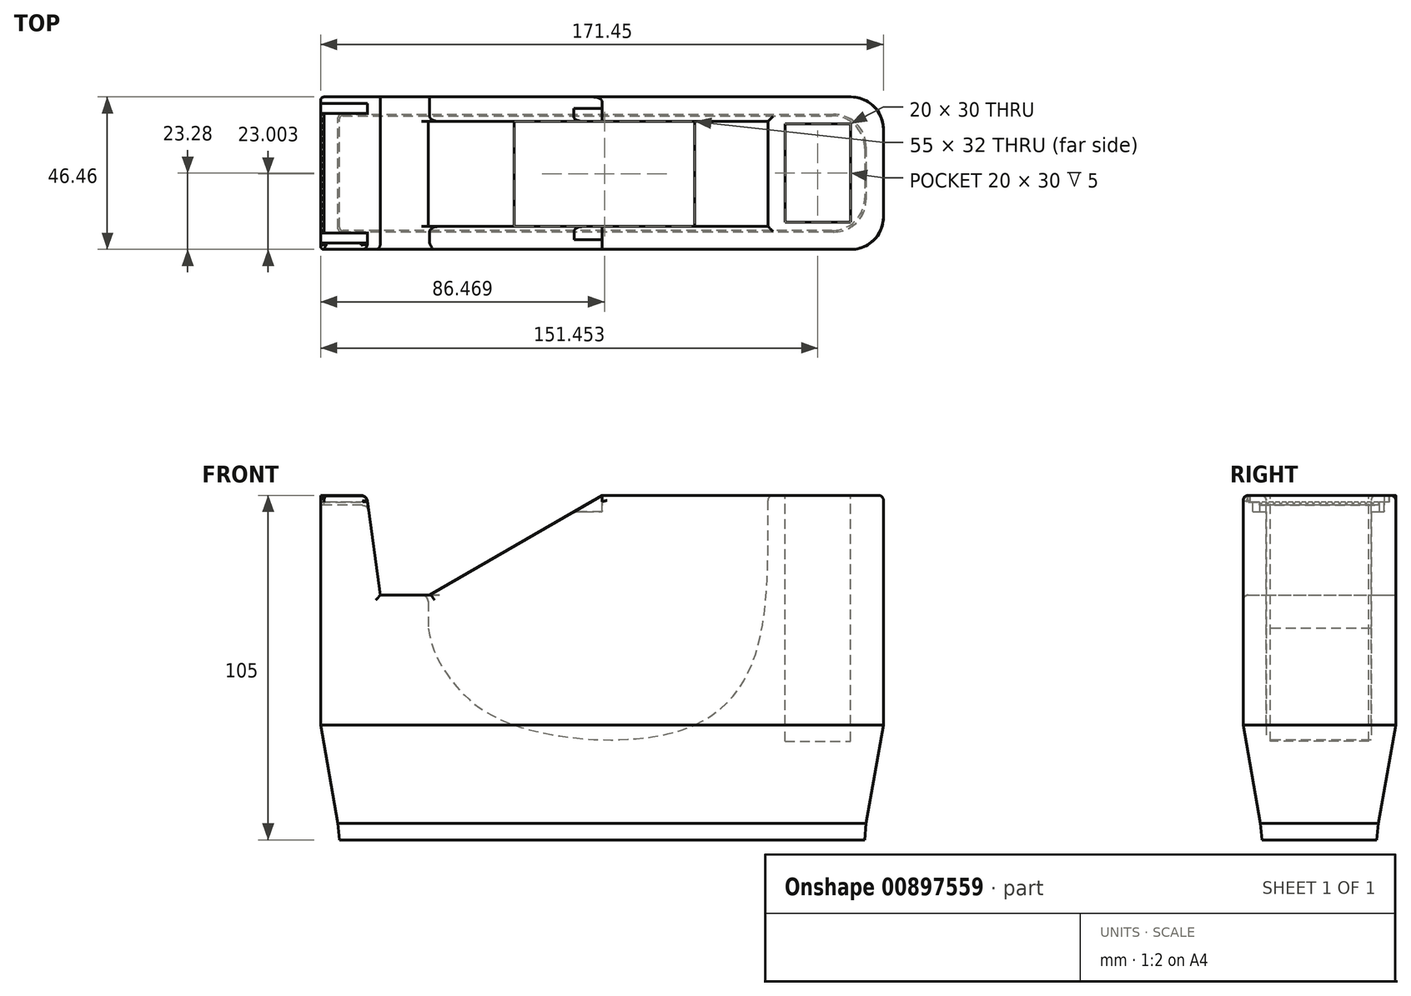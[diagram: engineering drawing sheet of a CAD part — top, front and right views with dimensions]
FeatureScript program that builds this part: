
annotation { "Feature Type Name" : "Feature", "Feature Type Description" : "" }
export const myFeature = defineFeature(function(context is Context, id is Id, definition is map)
    precondition{}
    {
        {
            var Q0;
            Q0=qCreatedBy(makeId("Top.planeOp"),FACE);
            var sketch = newSketch(context, id + "F0", { "sketchPlane" : qUnion([Q0])});
            skLineSegment(sketch, "E0.bottom", {"start": v(-80.11, 15.02) * mm, "end": v(79.89, 15.02) * mm});
            skLineSegment(sketch, "E0.top", {"start": v(-80.11, -19.98) * mm, "end": v(79.89, -19.98) * mm});
            skLineSegment(sketch, "E0.left", {"start": v(-80.11, 15.02) * mm, "end": v(-80.11, -19.98) * mm});
            skLineSegment(sketch, "E0.right", {"start": v(79.89, 15.02) * mm, "end": v(79.89, -19.98) * mm});
            skSolve(sketch);
        }
        {
            var Q0;
            Q0 = qSketchRegion(id + "F0", true);
            extrude(context, id + "F1", {"entities" : qUnion([Q0]), "depth" : 5 * mm, "offsetDistance" : 25 * mm, "hasDraft" : true, "draftAngle" : 5 * degree});
        }
        {
            var Q0;
            Q0=makeQuery(id+"F1.opExtrude","CAP_FACE",FACE,{"disambiguationData":[OSD([sQuery(id+"F0.wireOp",EDGE,"E0.bottom"),sQuery(id+"F0.wireOp",EDGE,"E0.top"),sQuery(id+"F0.wireOp",EDGE,"E0.left"),sQuery(id+"F0.wireOp",EDGE,"E0.right")])],"isStart":false});
            var sketch = newSketch(context, id + "F2", { "sketchPlane" : qUnion([Q0])});
            skLineSegment(sketch, "E1.bottom", {"start": v(-80.55, 15.46) * mm, "end": v(80.32, 15.46) * mm});
            skLineSegment(sketch, "E1.top", {"start": v(-80.55, -20.42) * mm, "end": v(80.32, -20.42) * mm});
            skLineSegment(sketch, "E1.left", {"start": v(-80.55, 15.46) * mm, "end": v(-80.55, -20.42) * mm});
            skLineSegment(sketch, "E1.right", {"start": v(80.32, 15.46) * mm, "end": v(80.32, -20.42) * mm});
            skSolve(sketch);
        }
        {
            var Q0;
            Q0 = qSketchRegion(id + "F2", true);
            extrude(context, id + "F3", {"entities" : qUnion([Q0]), "depth" : 30 * mm, "offsetDistance" : 25 * mm, "hasDraft" : true, "draftAngle" : 10 * degree});
        }
        {
            var Q0;
            Q0=makeQuery(id+"F3.opExtrude","CAP_FACE",FACE,{"disambiguationData":[OSD([sQuery(id+"F2.wireOp",EDGE,"E1.bottom"),sQuery(id+"F2.wireOp",EDGE,"E1.top"),sQuery(id+"F2.wireOp",EDGE,"E1.left"),sQuery(id+"F2.wireOp",EDGE,"E1.right")])],"isStart":false});
            var sketch = newSketch(context, id + "F4", { "sketchPlane" : qUnion([Q0])});
            skLineSegment(sketch, "E2.bottom", {"start": v(85.61, -25.7) * mm, "end": v(-85.84, -25.7) * mm});
            skLineSegment(sketch, "E2.top", {"start": v(85.61, 20.75) * mm, "end": v(-85.84, 20.75) * mm});
            skLineSegment(sketch, "E2.left", {"start": v(85.61, -25.7) * mm, "end": v(85.61, 20.75) * mm});
            skLineSegment(sketch, "E2.right", {"start": v(-85.84, -25.7) * mm, "end": v(-85.84, 20.75) * mm});
            skSolve(sketch);
        }
        {
            var Q0;
            Q0 = qSketchRegion(id + "F4", true);
            extrude(context, id + "F5", {"entities" : qUnion([Q0]), "depth" : 70 * mm, "offsetDistance" : 25 * mm});
        }
        {
            var Q0;
            Q0=makeQuery(id+"F5.opExtrude","SWEPT_FACE",FACE,{"disambiguationData":[OSD([sQuery(id+"F4.wireOp",EDGE,"E2.top")])]});
            var sketch = newSketch(context, id + "F6", { "sketchPlane" : qUnion([Q0])});
            skLineSegment(sketch, "E3", {"start": v(0.11, 105) * mm, "end": v(52.63, 74.68) * mm});
            skLineSegment(sketch, "E4", {"start": v(52.63, 74.68) * mm, "end": v(67.63, 74.68) * mm});
            skLineSegment(sketch, "E5", {"start": v(67.63, 74.68) * mm, "end": v(72.07, 106.96) * mm});
            skLineSegment(sketch, "E6", {"start": v(0.11, 105) * mm, "end": v(0.11, 119.16) * mm});
            skLineSegment(sketch, "E7", {"start": v(0.11, 119.16) * mm, "end": v(72.07, 119.16) * mm});
            skLineSegment(sketch, "E8", {"start": v(72.07, 119.16) * mm, "end": v(72.07, 106.96) * mm});
            skSolve(sketch);
        }
        {
            var Q0;
            Q0 = qSketchRegion(id + "F6", true);
            extrude(context, id + "F7", {"entities" : qUnion([Q0]), "operationType" : NewBodyOperationType.REMOVE, "endBound" : BoundingType.THROUGH_ALL, "oppositeDirection" : true, "depth" : 25 * mm, "offsetDistance" : 25 * mm, "hasDraft" : true, "draftAngle" : 0.1 * degree});
        }
        {
            var Q0;
            {var subQ0=sQuery(id+"F4.wireOp",EDGE,"E2.left");var subQ1=sQuery(id+"F4.wireOp",EDGE,"E2.top");var subQ2=sQuery(id+"F4.wireOp",EDGE,"E2.bottom");Q0=makeQuery(id+"F7.boolean.opBoolean","SPLIT",FACE,{"disambiguationData":[TD([makeQuery(id+"F5.opExtrude","SWEPT_FACE",FACE,{"disambiguationData":[OSD([subQ0])]})])],"derivedFrom":makeQuery(id+"F5.opExtrude","CAP_FACE",FACE,{"disambiguationData":[OSD([subQ2,subQ1,subQ0,sQuery(id+"F4.wireOp",EDGE,"E2.right")])],"isStart":false})});}
            var sketch = newSketch(context, id + "F8", { "sketchPlane" : qUnion([Q0])});
            skLineSegment(sketch, "E9.bottom", {"start": v(55.61, 12.57) * mm, "end": v(75.61, 12.57) * mm});
            skLineSegment(sketch, "E9.top", {"start": v(55.61, -17.43) * mm, "end": v(75.61, -17.43) * mm});
            skLineSegment(sketch, "E9.left", {"start": v(55.61, 12.57) * mm, "end": v(55.61, -17.43) * mm});
            skLineSegment(sketch, "E9.right", {"start": v(75.61, 12.57) * mm, "end": v(75.61, -17.43) * mm});
            skSolve(sketch);
        }
        {
            var Q0;
            Q0 = qSketchRegion(id + "F8", true);
            extrude(context, id + "F9", {"entities" : qUnion([Q0]), "operationType" : NewBodyOperationType.REMOVE, "oppositeDirection" : true, "depth" : 75 * mm, "offsetDistance" : 25 * mm});
        }
        {
            var Q0;
            {var subQ0=sQuery(id+"F4.wireOp",EDGE,"E2.bottom");var subQ1=sQuery(id+"F4.wireOp",EDGE,"E2.right");var subQ2=sQuery(id+"F4.wireOp",EDGE,"E2.top");Q0=makeQuery(id+"F7.boolean.opBoolean","SPLIT",FACE,{"disambiguationData":[TD([makeQuery(id+"F5.opExtrude","SWEPT_FACE",FACE,{"disambiguationData":[OSD([subQ1])]})])],"derivedFrom":makeQuery(id+"F5.opExtrude","CAP_FACE",FACE,{"disambiguationData":[OSD([subQ0,subQ2,sQuery(id+"F4.wireOp",EDGE,"E2.left"),subQ1])],"isStart":false})});}
            var sketch = newSketch(context, id + "F10", { "sketchPlane" : qUnion([Q0])});
            skLineSegment(sketch, "E10.bottom", {"start": v(-71.8, 15.75) * mm, "end": v(-83.4, 15.75) * mm});
            skLineSegment(sketch, "E10.top", {"start": v(-71.7, -20.7) * mm, "end": v(-85.84, -20.7) * mm});
            skLineSegment(sketch, "E11", {"start": v(-83.4, 15.75) * mm, "end": v(-86.58, 15.75) * mm});
            skLineSegment(sketch, "E12", {"start": v(-86.58, 15.75) * mm, "end": v(-86.58, -20.7) * mm});
            skLineSegment(sketch, "E13", {"start": v(-86.58, -20.7) * mm, "end": v(-67.93, -20.7) * mm});
            skLineSegment(sketch, "E14", {"start": v(-67.93, -20.7) * mm, "end": v(-67.93, 15.75) * mm});
            skLineSegment(sketch, "E15", {"start": v(-67.93, 15.75) * mm, "end": v(-71.8, 15.75) * mm});
            skSolve(sketch);
        }
        {
            var Q0;
            Q0 = qSketchRegion(id + "F10", true);
            extrude(context, id + "F11", {"entities" : qUnion([Q0]), "operationType" : NewBodyOperationType.REMOVE, "oppositeDirection" : true, "depth" : 3 * mm, "offsetDistance" : 25 * mm});
        }
        {
            var Q0;
            Q0=makeQuery(id+"F5.opExtrude","SWEPT_FACE",FACE,{"disambiguationData":[OSD([sQuery(id+"F4.wireOp",EDGE,"E2.bottom")])]});
            cPlane(context, id + "F12", {"entities" : qUnion([Q0]), "cplaneType" : CPlaneType.OFFSET, "offset" : 7 * mm, "oppositeDirection" : true, "width" : 150 * mm, "height" : 150 * mm});
        }
        {
            var Q0;
            Q0=qCreatedBy(id+"F12.planeOp",FACE);
            var sketch = newSketch(context, id + "F13", { "sketchPlane" : qUnion([Q0])});
            skLineSegment(sketch, "E16", {"start": v(50.39, 109.97) * mm, "end": v(-53.08, 109.97) * mm});
            skLineSegment(sketch, "E17", {"start": v(-53.08, 109.97) * mm, "end": v(-53.08, 64.4) * mm});
            skFitSpline(sketch, "E18", {"points": [v(-53.08, 64.4) * mm, v(-47.6, 50.9) * mm, v(-30.65, 36.48) * mm, v(24.3, 33.5) * mm, v(46.5, 56.17) * mm, v(50.39, 109.97) * mm], "startDerivative": vector(31.13, -150.45) * mm, "endDerivative": vector(-1.03, 260.97) * mm});
            skSolve(sketch);
        }
        {
            var Q0;
            Q0 = qSketchRegion(id + "F13", true);
            extrude(context, id + "F14", {"entities" : qUnion([Q0]), "operationType" : NewBodyOperationType.REMOVE, "oppositeDirection" : true, "depth" : 32 * mm, "offsetDistance" : 25 * mm});
        }
        {
            var Q0;
            Q0=makeQuery(id+"F14.boolean.opBoolean","COPY",FACE,{"derivedFrom":makeQuery(id+"F14.opExtrude","CAP_FACE",FACE,{"disambiguationData":[OSD([sQuery(id+"F13.wireOp",EDGE,"E16"),sQuery(id+"F13.wireOp",EDGE,"E17"),sQuery(id+"F13.wireOp",EDGE,"E18")])],"isStart":true})});
            var sketch = newSketch(context, id + "F15", { "sketchPlane" : qUnion([Q0])});
            skLineSegment(sketch, "E19", {"start": v(0.05, 105) * mm, "end": v(0.05, 100) * mm});
            skLineSegment(sketch, "E20", {"start": v(0.05, 100) * mm, "end": v(9.05, 100) * mm});
            skLineSegment(sketch, "E21", {"start": v(9.05, 100) * mm, "end": v(9.05, 103) * mm});
            skLineSegment(sketch, "E22", {"start": v(9.05, 103) * mm, "end": v(4.05, 103) * mm});
            skLineSegment(sketch, "E23", {"start": v(4.05, 103) * mm, "end": v(4.05, 105) * mm});
            skLineSegment(sketch, "E24", {"start": v(4.05, 105) * mm, "end": v(0.05, 105) * mm});
            skSolve(sketch);
        }
        {
            var Q0;
            Q0 = qSketchRegion(id + "F15", true);
            extrude(context, id + "F16", {"entities" : qUnion([Q0]), "operationType" : NewBodyOperationType.REMOVE, "oppositeDirection" : true, "depth" : 4 * mm, "offsetDistance" : 25 * mm, "hasSecondDirection" : true, "secondDirectionOppositeDirection" : false, "secondDirectionDepth" : 36 * mm});
        }
        {
            var Q0;
            Q0=makeQuery(id+"F5.opExtrude","SWEPT_FACE",FACE,{"disambiguationData":[OSD([sQuery(id+"F4.wireOp",EDGE,"E2.right")])]});
            var sketch = newSketch(context, id + "F17", { "sketchPlane" : qUnion([Q0])});
            skLineSegment(sketch, "E25", {"start": v(-15.75, 102) * mm, "end": v(-14.75, 105) * mm});
            skPoint(sketch, "E25.endSnap0", {"position": v(2.48, 105) * mm});
            skLineSegment(sketch, "E26", {"start": v(-14.75, 105) * mm, "end": v(-14.75, 102) * mm, "construction": true});
            skLineSegment(sketch, "E27", {"start": v(-15.75, 102) * mm, "end": v(-15.75, 97.68) * mm});
            skLineSegment(sketch, "E28", {"start": v(-15.75, 97.68) * mm, "end": v(20.7, 97.68) * mm});
            skLineSegment(sketch, "E29.MirrorCS", {"start": v(-13.75, 102) * mm, "end": v(-14.75, 105) * mm});
            skLineSegment(sketch, "E30.1.0.0", {"start": v(-11.75, 102) * mm, "end": v(-12.75, 105) * mm});
            skLineSegment(sketch, "E30.1.0.1", {"start": v(-13.75, 102) * mm, "end": v(-12.75, 105) * mm});
            skLineSegment(sketch, "E30.2.0.0", {"start": v(-9.75, 102) * mm, "end": v(-10.75, 105) * mm});
            skLineSegment(sketch, "E30.2.0.1", {"start": v(-11.75, 102) * mm, "end": v(-10.75, 105) * mm});
            skLineSegment(sketch, "E30.direction1", {"start": v(-13.75, 102) * mm, "end": v(-11.75, 102) * mm, "construction": true});
            skLineSegment(sketch, "E31.0.3.0", {"start": v(-7.75, 102) * mm, "end": v(-8.75, 105) * mm});
            skLineSegment(sketch, "E31.3.3.0", {"start": v(-9.75, 102) * mm, "end": v(-8.75, 105) * mm});
            skLineSegment(sketch, "E31.0.4.0", {"start": v(-5.75, 102) * mm, "end": v(-6.75, 105) * mm});
            skLineSegment(sketch, "E31.3.4.0", {"start": v(-7.75, 102) * mm, "end": v(-6.75, 105) * mm});
            skLineSegment(sketch, "E31.0.5.0", {"start": v(-3.75, 102) * mm, "end": v(-4.75, 105) * mm});
            skLineSegment(sketch, "E31.3.5.0", {"start": v(-5.75, 102) * mm, "end": v(-4.75, 105) * mm});
            skLineSegment(sketch, "E31.0.6.0", {"start": v(-1.75, 102) * mm, "end": v(-2.75, 105) * mm});
            skLineSegment(sketch, "E31.3.6.0", {"start": v(-3.75, 102) * mm, "end": v(-2.75, 105) * mm});
            skLineSegment(sketch, "E31.0.7.0", {"start": v(0.25, 102) * mm, "end": v(-0.75, 105) * mm});
            skLineSegment(sketch, "E31.3.7.0", {"start": v(-1.75, 102) * mm, "end": v(-0.75, 105) * mm});
            skLineSegment(sketch, "E31.0.8.0", {"start": v(2.25, 102) * mm, "end": v(1.25, 105) * mm});
            skLineSegment(sketch, "E31.3.8.0", {"start": v(0.25, 102) * mm, "end": v(1.25, 105) * mm});
            skLineSegment(sketch, "E31.0.9.0", {"start": v(4.25, 102) * mm, "end": v(3.25, 105) * mm});
            skLineSegment(sketch, "E31.3.9.0", {"start": v(2.25, 102) * mm, "end": v(3.25, 105) * mm});
            skLineSegment(sketch, "E31.0.10.0", {"start": v(6.25, 102) * mm, "end": v(5.25, 105) * mm});
            skLineSegment(sketch, "E31.3.10.0", {"start": v(4.25, 102) * mm, "end": v(5.25, 105) * mm});
            skLineSegment(sketch, "E31.0.11.0", {"start": v(8.25, 102) * mm, "end": v(7.25, 105) * mm});
            skLineSegment(sketch, "E31.3.11.0", {"start": v(6.25, 102) * mm, "end": v(7.25, 105) * mm});
            skLineSegment(sketch, "E32.0.12.0", {"start": v(10.25, 102) * mm, "end": v(9.25, 105) * mm});
            skLineSegment(sketch, "E32.3.12.0", {"start": v(8.25, 102) * mm, "end": v(9.25, 105) * mm});
            skLineSegment(sketch, "E32.0.13.0", {"start": v(12.25, 102) * mm, "end": v(11.25, 105) * mm});
            skLineSegment(sketch, "E32.3.13.0", {"start": v(10.25, 102) * mm, "end": v(11.25, 105) * mm});
            skLineSegment(sketch, "E33.0.14.0", {"start": v(14.25, 102) * mm, "end": v(13.25, 105) * mm});
            skLineSegment(sketch, "E33.3.14.0", {"start": v(12.25, 102) * mm, "end": v(13.25, 105) * mm});
            skLineSegment(sketch, "E34.0.15.0", {"start": v(16.25, 102) * mm, "end": v(15.25, 105) * mm});
            skLineSegment(sketch, "E34.3.15.0", {"start": v(14.25, 102) * mm, "end": v(15.25, 105) * mm});
            skLineSegment(sketch, "E34.0.16.0", {"start": v(18.25, 102) * mm, "end": v(17.25, 105) * mm});
            skLineSegment(sketch, "E34.3.16.0", {"start": v(16.25, 102) * mm, "end": v(17.25, 105) * mm});
            skLineSegment(sketch, "E35.0.17.0", {"start": v(20.25, 102) * mm, "end": v(19.25, 105) * mm});
            skLineSegment(sketch, "E35.3.17.0", {"start": v(18.25, 102) * mm, "end": v(19.25, 105) * mm});
            skLineSegment(sketch, "E36", {"start": v(20.7, 97.68) * mm, "end": v(20.25, 102) * mm});
            skSolve(sketch);
        }
        {
            var Q0;
            Q0 = qSketchRegion(id + "F17", true);
            extrude(context, id + "F18", {"entities" : qUnion([Q0]), "operationType" : NewBodyOperationType.ADD, "oppositeDirection" : true, "depth" : 1 * mm, "offsetDistance" : 25 * mm});
        }
        {
            var Q0;
            Q0=makeQuery(id+"F5.opExtrude","SWEPT_EDGE",EDGE,{"disambiguationData":[OSD([sQuery(id+"F4.wireOp",EDGE,"E2.top"),sQuery(id+"F4.wireOp",EDGE,"E2.right")])]});
            var Q1;
            Q1=makeQuery(id+"F3.opExtrude","SWEPT_EDGE",EDGE,{"disambiguationData":[OSD([sQuery(id+"F2.wireOp",EDGE,"E1.bottom"),sQuery(id+"F2.wireOp",EDGE,"E1.left")])]});
            var Q2;
            Q2=makeQuery(id+"F5.opExtrude","SWEPT_EDGE",EDGE,{"disambiguationData":[OSD([sQuery(id+"F4.wireOp",EDGE,"E2.bottom"),sQuery(id+"F4.wireOp",EDGE,"E2.right")])]});
            var Q3;
            Q3=makeQuery(id+"F3.opExtrude","SWEPT_EDGE",EDGE,{"disambiguationData":[OSD([sQuery(id+"F2.wireOp",EDGE,"E1.top"),sQuery(id+"F2.wireOp",EDGE,"E1.left")])]});
            var Q4;
            Q4=makeQuery(id+"F1.opExtrude","SWEPT_EDGE",EDGE,{"disambiguationData":[OSD([sQuery(id+"F0.wireOp",EDGE,"E0.top"),sQuery(id+"F0.wireOp",EDGE,"E0.left")])]});
            var Q5;
            Q5=makeQuery(id+"F1.opExtrude","SWEPT_EDGE",EDGE,{"disambiguationData":[OSD([sQuery(id+"F0.wireOp",EDGE,"E0.bottom"),sQuery(id+"F0.wireOp",EDGE,"E0.left")])]});
            fillet(context, id + "F19", {"entities" : qUnion([Q0, Q1, Q2, Q3, Q4, Q5]), "radius" : 1 * mm, "tangentPropagation" : true, "allowEdgeOverflow" : false});
        }
        {
            var Q0;
            Q0=makeQuery(id+"F5.opExtrude","CAP_EDGE",EDGE,{"disambiguationData":[OSD([sQuery(id+"F4.wireOp",EDGE,"E2.left")])],"isStart":false});
            var Q1;
            {var subQ0=sQuery(id+"F4.wireOp",EDGE,"E2.bottom");var subQ1=sQuery(id+"F4.wireOp",EDGE,"E2.left");Q1=makeQuery(id+"F7.boolean.opBoolean","SPLIT",EDGE,{"disambiguationData":[TD([makeQuery(id+"F5.opExtrude","SWEPT_FACE",FACE,{"disambiguationData":[OSD([subQ1])]})])],"derivedFrom":makeQuery(id+"F5.opExtrude","CAP_EDGE",EDGE,{"disambiguationData":[OSD([subQ0])],"isStart":false})});}
            var Q2;
            {var subQ0=sQuery(id+"F4.wireOp",EDGE,"E2.left");var subQ1=sQuery(id+"F4.wireOp",EDGE,"E2.top");var subQ2=sQuery(id+"F4.wireOp",EDGE,"E2.bottom");Q2=makeQuery(id+"F19.opFillet","BLEND_EDGE",EDGE,{"blendedFrom":[makeQuery(id+"F5.opExtrude","SWEPT_EDGE",EDGE,{"disambiguationData":[OSD([subQ2,subQ0])]}),makeQuery(id+"F7.boolean.opBoolean","SPLIT",FACE,{"disambiguationData":[TD([makeQuery(id+"F5.opExtrude","SWEPT_FACE",FACE,{"disambiguationData":[OSD([subQ0])]})])],"derivedFrom":makeQuery(id+"F5.opExtrude","CAP_FACE",FACE,{"disambiguationData":[OSD([subQ2,subQ1,subQ0,sQuery(id+"F4.wireOp",EDGE,"E2.right")])],"isStart":false})})],"blendedInto":[makeQuery(id+"F7.boolean.opBoolean","SPLIT",FACE,{"disambiguationData":[TD([makeQuery(id+"F5.opExtrude","SWEPT_FACE",FACE,{"disambiguationData":[OSD([subQ0])]})])],"derivedFrom":makeQuery(id+"F5.opExtrude","CAP_FACE",FACE,{"disambiguationData":[OSD([subQ2,subQ1,subQ0,sQuery(id+"F4.wireOp",EDGE,"E2.right")])],"isStart":false})})]});}
            var Q3;
            {var subQ0=sQuery(id+"F4.wireOp",EDGE,"E2.left");var subQ1=sQuery(id+"F4.wireOp",EDGE,"E2.top");var subQ2=sQuery(id+"F4.wireOp",EDGE,"E2.bottom");Q3=makeQuery(id+"F19.opFillet","BLEND_EDGE",EDGE,{"blendedFrom":[makeQuery(id+"F5.opExtrude","SWEPT_EDGE",EDGE,{"disambiguationData":[OSD([subQ1,subQ0])]}),makeQuery(id+"F7.boolean.opBoolean","SPLIT",FACE,{"disambiguationData":[TD([makeQuery(id+"F5.opExtrude","SWEPT_FACE",FACE,{"disambiguationData":[OSD([subQ0])]})])],"derivedFrom":makeQuery(id+"F5.opExtrude","CAP_FACE",FACE,{"disambiguationData":[OSD([subQ2,subQ1,subQ0,sQuery(id+"F4.wireOp",EDGE,"E2.right")])],"isStart":false})})],"blendedInto":[makeQuery(id+"F7.boolean.opBoolean","SPLIT",FACE,{"disambiguationData":[TD([makeQuery(id+"F5.opExtrude","SWEPT_FACE",FACE,{"disambiguationData":[OSD([subQ0])]})])],"derivedFrom":makeQuery(id+"F5.opExtrude","CAP_FACE",FACE,{"disambiguationData":[OSD([subQ2,subQ1,subQ0,sQuery(id+"F4.wireOp",EDGE,"E2.right")])],"isStart":false})})]});}
            var Q4;
            {var subQ0=sQuery(id+"F4.wireOp",EDGE,"E2.left");var subQ1=sQuery(id+"F4.wireOp",EDGE,"E2.top");Q4=makeQuery(id+"F7.boolean.opBoolean","SPLIT",EDGE,{"disambiguationData":[TD([makeQuery(id+"F5.opExtrude","SWEPT_FACE",FACE,{"disambiguationData":[OSD([subQ0])]})])],"derivedFrom":makeQuery(id+"F5.opExtrude","CAP_EDGE",EDGE,{"disambiguationData":[OSD([subQ1])],"isStart":false})});}
            var Q5;
            Q5=makeQuery(id+"F7.boolean.opBoolean","COPY",EDGE,{"derivedFrom":makeQuery(id+"F7.opExtrude","CAP_EDGE",EDGE,{"disambiguationData":[OSD([sQuery(id+"F6.wireOp",EDGE,"E4")])],"isStart":true})});
            var Q6;
            Q6=makeQuery(id+"F7.boolean.opBoolean","INTERSECT",EDGE,{"derivedFrom":[makeQuery(id+"F5.opExtrude","SWEPT_FACE",FACE,{"disambiguationData":[OSD([sQuery(id+"F4.wireOp",EDGE,"E2.bottom")])]}),makeQuery(id+"F7.opExtrude","SWEPT_FACE",FACE,{"disambiguationData":[OSD([sQuery(id+"F6.wireOp",EDGE,"E4")])]})]});
            var Q7;
            Q7=makeQuery(id+"F7.boolean.opBoolean","INTERSECT",EDGE,{"derivedFrom":[makeQuery(id+"F5.opExtrude","SWEPT_FACE",FACE,{"disambiguationData":[OSD([sQuery(id+"F4.wireOp",EDGE,"E2.bottom")])]}),makeQuery(id+"F7.opExtrude","SWEPT_FACE",FACE,{"disambiguationData":[OSD([sQuery(id+"F6.wireOp",EDGE,"E5")])]})]});
            var Q8;
            Q8=makeQuery(id+"F7.boolean.opBoolean","COPY",EDGE,{"derivedFrom":makeQuery(id+"F7.opExtrude","CAP_EDGE",EDGE,{"disambiguationData":[OSD([sQuery(id+"F6.wireOp",EDGE,"E5")])],"isStart":true})});
            var Q9;
            Q9=makeQuery(id+"F14.boolean.opBoolean","INTERSECT",EDGE,{"derivedFrom":[makeQuery(id+"F7.boolean.opBoolean","COPY",FACE,{"derivedFrom":makeQuery(id+"F7.opExtrude","SWEPT_FACE",FACE,{"disambiguationData":[OSD([sQuery(id+"F6.wireOp",EDGE,"E3")])]})}),makeQuery(id+"F14.opExtrude","CAP_FACE",FACE,{"disambiguationData":[OSD([sQuery(id+"F13.wireOp",EDGE,"E16"),sQuery(id+"F13.wireOp",EDGE,"E17"),sQuery(id+"F13.wireOp",EDGE,"E18")])],"isStart":false})]});
            var Q10;
            {var subQ0=sQuery(id+"F4.wireOp",EDGE,"E2.left");var subQ1=sQuery(id+"F4.wireOp",EDGE,"E2.top");var subQ2=sQuery(id+"F4.wireOp",EDGE,"E2.bottom");Q10=makeQuery(id+"F14.boolean.opBoolean","INTERSECT",EDGE,{"derivedFrom":[makeQuery(id+"F7.boolean.opBoolean","SPLIT",FACE,{"disambiguationData":[TD([makeQuery(id+"F5.opExtrude","SWEPT_FACE",FACE,{"disambiguationData":[OSD([subQ0])]})])],"derivedFrom":makeQuery(id+"F5.opExtrude","CAP_FACE",FACE,{"disambiguationData":[OSD([subQ2,subQ1,subQ0,sQuery(id+"F4.wireOp",EDGE,"E2.right")])],"isStart":false})}),makeQuery(id+"F14.opExtrude","CAP_FACE",FACE,{"disambiguationData":[OSD([sQuery(id+"F13.wireOp",EDGE,"E16"),sQuery(id+"F13.wireOp",EDGE,"E17"),sQuery(id+"F13.wireOp",EDGE,"E18")])],"isStart":false})]});}
            var Q11;
            {var subQ0=sQuery(id+"F4.wireOp",EDGE,"E2.left");var subQ1=sQuery(id+"F4.wireOp",EDGE,"E2.top");var subQ2=sQuery(id+"F4.wireOp",EDGE,"E2.bottom");Q11=makeQuery(id+"F14.boolean.opBoolean","INTERSECT",EDGE,{"derivedFrom":[makeQuery(id+"F7.boolean.opBoolean","SPLIT",FACE,{"disambiguationData":[TD([makeQuery(id+"F5.opExtrude","SWEPT_FACE",FACE,{"disambiguationData":[OSD([subQ0])]})])],"derivedFrom":makeQuery(id+"F5.opExtrude","CAP_FACE",FACE,{"disambiguationData":[OSD([subQ2,subQ1,subQ0,sQuery(id+"F4.wireOp",EDGE,"E2.right")])],"isStart":false})}),makeQuery(id+"F14.opExtrude","SWEPT_FACE",FACE,{"disambiguationData":[OSD([sQuery(id+"F13.wireOp",EDGE,"E18")])]})]});}
            var Q12;
            {var subQ0=sQuery(id+"F4.wireOp",EDGE,"E2.left");var subQ1=sQuery(id+"F4.wireOp",EDGE,"E2.top");var subQ2=sQuery(id+"F4.wireOp",EDGE,"E2.bottom");Q12=makeQuery(id+"F14.boolean.opBoolean","INTERSECT",EDGE,{"derivedFrom":[makeQuery(id+"F7.boolean.opBoolean","SPLIT",FACE,{"disambiguationData":[TD([makeQuery(id+"F5.opExtrude","SWEPT_FACE",FACE,{"disambiguationData":[OSD([subQ0])]})])],"derivedFrom":makeQuery(id+"F5.opExtrude","CAP_FACE",FACE,{"disambiguationData":[OSD([subQ2,subQ1,subQ0,sQuery(id+"F4.wireOp",EDGE,"E2.right")])],"isStart":false})}),makeQuery(id+"F14.opExtrude","CAP_FACE",FACE,{"disambiguationData":[OSD([sQuery(id+"F13.wireOp",EDGE,"E16"),sQuery(id+"F13.wireOp",EDGE,"E17"),sQuery(id+"F13.wireOp",EDGE,"E18")])],"isStart":true})]});}
            var Q13;
            Q13=makeQuery(id+"F14.boolean.opBoolean","INTERSECT",EDGE,{"derivedFrom":[makeQuery(id+"F7.boolean.opBoolean","COPY",FACE,{"derivedFrom":makeQuery(id+"F7.opExtrude","SWEPT_FACE",FACE,{"disambiguationData":[OSD([sQuery(id+"F6.wireOp",EDGE,"E3")])]})}),makeQuery(id+"F14.opExtrude","CAP_FACE",FACE,{"disambiguationData":[OSD([sQuery(id+"F13.wireOp",EDGE,"E16"),sQuery(id+"F13.wireOp",EDGE,"E17"),sQuery(id+"F13.wireOp",EDGE,"E18")])],"isStart":true})]});
            var Q14;
            Q14=makeQuery(id+"FTQLdfmlFeniJXV_1.boolean.opBoolean","MERGE",EDGE,{"derivedFrom":[makeQuery(id+"F9.boolean.opBoolean","COPY",EDGE,{"derivedFrom":makeQuery(id+"F9.opExtrude","CAP_EDGE",EDGE,{"disambiguationData":[OSD([sQuery(id+"F8.wireOp",EDGE,"E9.left")])],"isStart":true})})],"fromTools":[makeQuery(id+"FTQLdfmlFeniJXV_1.opExtrude","CAP_EDGE",EDGE,{"disambiguationData":[OSD([sQuery(id+"FKzSX45Tkruo3SP_1.wireOp",EDGE,"E9PlW4vk-rjUq-K3qM-MrI8-yHAp994fyExz.left")])],"isStart":true})]});
            var Q15;
            Q15=makeQuery(id+"FTQLdfmlFeniJXV_1.boolean.opBoolean","COPY",EDGE,{"derivedFrom":makeQuery(id+"FTQLdfmlFeniJXV_1.opExtrude","CAP_EDGE",EDGE,{"disambiguationData":[OSD([sQuery(id+"FKzSX45Tkruo3SP_1.wireOp",EDGE,"E9PlW4vk-rjUq-K3qM-MrI8-yHAp994fyExz.bottom")])],"isStart":true})});
            var Q16;
            Q16=makeQuery(id+"FTQLdfmlFeniJXV_1.boolean.opBoolean","COPY",EDGE,{"derivedFrom":makeQuery(id+"FTQLdfmlFeniJXV_1.opExtrude","CAP_EDGE",EDGE,{"disambiguationData":[OSD([sQuery(id+"FKzSX45Tkruo3SP_1.wireOp",EDGE,"E9PlW4vk-rjUq-K3qM-MrI8-yHAp994fyExz.right")])],"isStart":true})});
            var Q17;
            Q17=makeQuery(id+"FTQLdfmlFeniJXV_1.boolean.opBoolean","COPY",EDGE,{"derivedFrom":makeQuery(id+"FTQLdfmlFeniJXV_1.opExtrude","CAP_EDGE",EDGE,{"disambiguationData":[OSD([sQuery(id+"FKzSX45Tkruo3SP_1.wireOp",EDGE,"E9PlW4vk-rjUq-K3qM-MrI8-yHAp994fyExz.top")])],"isStart":true})});
            var Q18;
            Q18=makeQuery(id+"FTQLdfmlFeniJXV_1.boolean.opBoolean","COPY",EDGE,{"derivedFrom":makeQuery(id+"FTQLdfmlFeniJXV_1.opExtrude","SWEPT_EDGE",EDGE,{"disambiguationData":[OSD([sQuery(id+"FKzSX45Tkruo3SP_1.wireOp",EDGE,"E9PlW4vk-rjUq-K3qM-MrI8-yHAp994fyExz.top"),sQuery(id+"FKzSX45Tkruo3SP_1.wireOp",EDGE,"E9PlW4vk-rjUq-K3qM-MrI8-yHAp994fyExz.left")])]})});
            var Q19;
            Q19=makeQuery(id+"FTQLdfmlFeniJXV_1.boolean.opBoolean","COPY",EDGE,{"derivedFrom":makeQuery(id+"FTQLdfmlFeniJXV_1.opExtrude","SWEPT_EDGE",EDGE,{"disambiguationData":[OSD([sQuery(id+"FKzSX45Tkruo3SP_1.wireOp",EDGE,"E9PlW4vk-rjUq-K3qM-MrI8-yHAp994fyExz.bottom"),sQuery(id+"FKzSX45Tkruo3SP_1.wireOp",EDGE,"E9PlW4vk-rjUq-K3qM-MrI8-yHAp994fyExz.left")])]})});
            var Q20;
            Q20=makeQuery(id+"FTQLdfmlFeniJXV_1.boolean.opBoolean","COPY",EDGE,{"derivedFrom":makeQuery(id+"FTQLdfmlFeniJXV_1.opExtrude","SWEPT_EDGE",EDGE,{"disambiguationData":[OSD([sQuery(id+"FKzSX45Tkruo3SP_1.wireOp",EDGE,"E9PlW4vk-rjUq-K3qM-MrI8-yHAp994fyExz.bottom"),sQuery(id+"FKzSX45Tkruo3SP_1.wireOp",EDGE,"E9PlW4vk-rjUq-K3qM-MrI8-yHAp994fyExz.right")])]})});
            var Q21;
            Q21=makeQuery(id+"FTQLdfmlFeniJXV_1.boolean.opBoolean","COPY",EDGE,{"derivedFrom":makeQuery(id+"FTQLdfmlFeniJXV_1.opExtrude","SWEPT_EDGE",EDGE,{"disambiguationData":[OSD([sQuery(id+"FKzSX45Tkruo3SP_1.wireOp",EDGE,"E9PlW4vk-rjUq-K3qM-MrI8-yHAp994fyExz.top"),sQuery(id+"FKzSX45Tkruo3SP_1.wireOp",EDGE,"E9PlW4vk-rjUq-K3qM-MrI8-yHAp994fyExz.right")])]})});
            fillet(context, id + "F20", {"entities" : qUnion([Q0, Q1, Q2, Q3, Q4, Q5, Q6, Q7, Q8, Q9, Q10, Q11, Q12, Q13, Q14, Q15, Q16, Q17, Q18, Q19, Q20, Q21]), "radius" : 1.5 * mm, "tangentPropagation" : true, "allowEdgeOverflow" : false});
        }
        {
            var Q0;
            Q0=makeQuery(id+"F7.boolean.opBoolean","INTERSECT",EDGE,{"derivedFrom":[makeQuery(id+"F5.opExtrude","SWEPT_FACE",FACE,{"disambiguationData":[OSD([sQuery(id+"F4.wireOp",EDGE,"E2.bottom")])]}),makeQuery(id+"F7.opExtrude","SWEPT_FACE",FACE,{"disambiguationData":[OSD([sQuery(id+"F6.wireOp",EDGE,"E3")])]})]});
            var Q1;
            Q1=makeQuery(id+"F7.boolean.opBoolean","COPY",EDGE,{"derivedFrom":makeQuery(id+"F7.opExtrude","CAP_EDGE",EDGE,{"disambiguationData":[OSD([sQuery(id+"F6.wireOp",EDGE,"E3")])],"isStart":true})});
            var Q2;
            Q2=makeQuery(id+"F14.boolean.opBoolean","INTERSECT",EDGE,{"derivedFrom":[makeQuery(id+"F7.boolean.opBoolean","COPY",FACE,{"derivedFrom":makeQuery(id+"F7.opExtrude","SWEPT_FACE",FACE,{"disambiguationData":[OSD([sQuery(id+"F6.wireOp",EDGE,"E4")])]})}),makeQuery(id+"F14.opExtrude","SWEPT_FACE",FACE,{"disambiguationData":[OSD([sQuery(id+"F13.wireOp",EDGE,"E17")])]})]});
            var Q3;
            Q3=makeQuery(id+"F11.boolean.opBoolean","INTERSECT",EDGE,{"derivedFrom":[makeQuery(id+"F7.boolean.opBoolean","COPY",FACE,{"derivedFrom":makeQuery(id+"F7.opExtrude","SWEPT_FACE",FACE,{"disambiguationData":[OSD([sQuery(id+"F6.wireOp",EDGE,"E5")])]})}),makeQuery(id+"F11.opExtrude","CAP_FACE",FACE,{"disambiguationData":[OSD([sQuery(id+"F10.wireOp",EDGE,"E10.bottom"),sQuery(id+"F10.wireOp",EDGE,"E11"),sQuery(id+"F10.wireOp",EDGE,"E12"),sQuery(id+"F10.wireOp",EDGE,"E13"),sQuery(id+"F10.wireOp",EDGE,"E14"),sQuery(id+"F10.wireOp",EDGE,"E15")])],"isStart":false})]});
            var Q4;
            Q4=makeQuery(id+"F11.boolean.opBoolean","COPY",EDGE,{"derivedFrom":makeQuery(id+"F11.opExtrude","CAP_EDGE",EDGE,{"disambiguationData":[OSD([sQuery(id+"F10.wireOp",EDGE,"E10.bottom"),sQuery(id+"F10.wireOp",EDGE,"E11"),sQuery(id+"F10.wireOp",EDGE,"E15")])],"isStart":true})});
            var Q5;
            Q5=makeQuery(id+"F11.boolean.opBoolean","COPY",EDGE,{"derivedFrom":makeQuery(id+"F11.opExtrude","CAP_EDGE",EDGE,{"disambiguationData":[OSD([sQuery(id+"F10.wireOp",EDGE,"E13")])],"isStart":true})});
            var Q6;
            {var subQ0=sQuery(id+"F4.wireOp",EDGE,"E2.top");var subQ1=makeQuery(id+"F5.opExtrude","CAP_FACE",FACE,{"disambiguationData":[OSD([sQuery(id+"F4.wireOp",EDGE,"E2.bottom"),subQ0,sQuery(id+"F4.wireOp",EDGE,"E2.left"),sQuery(id+"F4.wireOp",EDGE,"E2.right")])],"isStart":false});var subQ2=makeQuery(id+"F7.opExtrude","SWEPT_FACE",FACE,{"disambiguationData":[OSD([sQuery(id+"F6.wireOp",EDGE,"E5")])]});Q6=makeQuery(id+"F11.boolean.opBoolean","SPLIT",EDGE,{"disambiguationData":[TD([makeQuery(id+"F5.opExtrude","SWEPT_FACE",FACE,{"disambiguationData":[OSD([subQ0])]})])],"derivedFrom":makeQuery(id+"F7.boolean.opBoolean","INTERSECT",EDGE,{"derivedFrom":[subQ1,subQ2]})});}
            var Q7;
            {var subQ0=sQuery(id+"F4.wireOp",EDGE,"E2.bottom");var subQ1=makeQuery(id+"F7.opExtrude","SWEPT_FACE",FACE,{"disambiguationData":[OSD([sQuery(id+"F6.wireOp",EDGE,"E5")])]});var subQ2=makeQuery(id+"F5.opExtrude","CAP_FACE",FACE,{"disambiguationData":[OSD([subQ0,sQuery(id+"F4.wireOp",EDGE,"E2.top"),sQuery(id+"F4.wireOp",EDGE,"E2.left"),sQuery(id+"F4.wireOp",EDGE,"E2.right")])],"isStart":false});Q7=makeQuery(id+"F11.boolean.opBoolean","SPLIT",EDGE,{"disambiguationData":[TD([makeQuery(id+"F5.opExtrude","SWEPT_FACE",FACE,{"disambiguationData":[OSD([subQ0])]})])],"derivedFrom":makeQuery(id+"F7.boolean.opBoolean","INTERSECT",EDGE,{"derivedFrom":[subQ2,subQ1]})});}
            fillet(context, id + "F21", {"entities" : qUnion([Q0, Q1, Q2, Q3, Q4, Q5, Q6, Q7]), "radius" : 2 * mm, "tangentPropagation" : true, "allowEdgeOverflow" : false});
        }
        {
            var Q0;
            Q0=makeQuery(id+"F5.opExtrude","SWEPT_EDGE",EDGE,{"disambiguationData":[OSD([sQuery(id+"F4.wireOp",EDGE,"E2.bottom"),sQuery(id+"F4.wireOp",EDGE,"E2.left")])]});
            var Q1;
            Q1=makeQuery(id+"F3.opExtrude","SWEPT_EDGE",EDGE,{"disambiguationData":[OSD([sQuery(id+"F2.wireOp",EDGE,"E1.top"),sQuery(id+"F2.wireOp",EDGE,"E1.right")])]});
            var Q2;
            Q2=makeQuery(id+"F1.opExtrude","SWEPT_EDGE",EDGE,{"disambiguationData":[OSD([sQuery(id+"F0.wireOp",EDGE,"E0.top"),sQuery(id+"F0.wireOp",EDGE,"E0.right")])]});
            var Q3;
            Q3=makeQuery(id+"F5.opExtrude","SWEPT_EDGE",EDGE,{"disambiguationData":[OSD([sQuery(id+"F4.wireOp",EDGE,"E2.top"),sQuery(id+"F4.wireOp",EDGE,"E2.left")])]});
            var Q4;
            Q4=makeQuery(id+"F3.opExtrude","SWEPT_EDGE",EDGE,{"disambiguationData":[OSD([sQuery(id+"F2.wireOp",EDGE,"E1.bottom"),sQuery(id+"F2.wireOp",EDGE,"E1.right")])]});
            var Q5;
            Q5=makeQuery(id+"F1.opExtrude","SWEPT_EDGE",EDGE,{"disambiguationData":[OSD([sQuery(id+"F0.wireOp",EDGE,"E0.bottom"),sQuery(id+"F0.wireOp",EDGE,"E0.right")])]});
            fillet(context, id + "F22", {"entities" : qUnion([Q0, Q1, Q2, Q3, Q4, Q5]), "radius" : 10 * mm, "tangentPropagation" : true, "allowEdgeOverflow" : false});
        }
        {
            var Q0;
            {var subQ0=sQuery(id+"F4.wireOp",EDGE,"E2.bottom");var subQ1=sQuery(id+"F4.wireOp",EDGE,"E2.right");var subQ2=sQuery(id+"F4.wireOp",EDGE,"E2.top");Q0=makeQuery(id+"F7.boolean.opBoolean","SPLIT",FACE,{"disambiguationData":[TD([makeQuery(id+"F5.opExtrude","SWEPT_FACE",FACE,{"disambiguationData":[OSD([subQ1])]})])],"derivedFrom":makeQuery(id+"F5.opExtrude","CAP_FACE",FACE,{"disambiguationData":[OSD([subQ0,subQ2,sQuery(id+"F4.wireOp",EDGE,"E2.left"),subQ1])],"isStart":false})});}
            var sketch = newSketch(context, id + "F23", { "sketchPlane" : qUnion([Q0])});
            skLineSegment(sketch, "E37.bottom", {"start": v(-70.28, 18.75) * mm, "end": v(-86.28, 18.75) * mm});
            skLineSegment(sketch, "E37.top", {"start": v(-70.28, -23.7) * mm, "end": v(-86.28, -23.7) * mm});
            skLineSegment(sketch, "E37.left", {"start": v(-70.28, 18.75) * mm, "end": v(-70.28, -23.7) * mm});
            skLineSegment(sketch, "E37.right", {"start": v(-86.28, 18.75) * mm, "end": v(-86.28, -23.7) * mm});
            skSolve(sketch);
        }
        {
            var Q0;
            Q0 = qSketchRegion(id + "F23", true);
            extrude(context, id + "F24", {"entities" : qUnion([Q0]), "operationType" : NewBodyOperationType.REMOVE, "oppositeDirection" : true, "depth" : 2 * mm, "offsetDistance" : 25 * mm});
        }
        {
            var Q0;
            {var subQ0=sQuery(id+"F4.wireOp",EDGE,"E2.bottom");var subQ1=sQuery(id+"F4.wireOp",EDGE,"E2.right");var subQ2=makeQuery(id+"F5.opExtrude","SWEPT_FACE",FACE,{"disambiguationData":[OSD([subQ1])]});var subQ3=sQuery(id+"F4.wireOp",EDGE,"E2.top");var subQ6=makeQuery(id+"F5.opExtrude","CAP_FACE",FACE,{"disambiguationData":[OSD([subQ0,subQ3,sQuery(id+"F4.wireOp",EDGE,"E2.left"),subQ1])],"isStart":false});Q0=makeQuery(id+"F24.boolean.opBoolean","MERGE",EDGE,{"derivedFrom":[makeQuery(id+"F21.opFillet","BLEND_EDGE",EDGE,{"blendedFrom":[makeQuery(id+"F7.boolean.opBoolean","SPLIT",EDGE,{"disambiguationData":[TD([subQ2])],"derivedFrom":makeQuery(id+"F5.opExtrude","CAP_EDGE",EDGE,{"disambiguationData":[OSD([subQ3])],"isStart":false})}),makeQuery(id+"F7.boolean.opBoolean","SPLIT",FACE,{"disambiguationData":[TD([subQ2])],"derivedFrom":subQ6})],"blendedInto":[makeQuery(id+"F7.boolean.opBoolean","SPLIT",FACE,{"disambiguationData":[TD([subQ2])],"derivedFrom":subQ6})]})],"fromTools":[makeQuery(id+"F24.opExtrude","CAP_EDGE",EDGE,{"disambiguationData":[OSD([sQuery(id+"F23.wireOp",EDGE,"E37.bottom")])],"isStart":true})]});}
            var Q1;
            {var subQ0=sQuery(id+"F4.wireOp",EDGE,"E2.bottom");var subQ2=sQuery(id+"F4.wireOp",EDGE,"E2.right");var subQ3=makeQuery(id+"F5.opExtrude","SWEPT_FACE",FACE,{"disambiguationData":[OSD([subQ2])]});var subQ4=sQuery(id+"F4.wireOp",EDGE,"E2.top");var subQ6=makeQuery(id+"F5.opExtrude","CAP_FACE",FACE,{"disambiguationData":[OSD([subQ0,subQ4,sQuery(id+"F4.wireOp",EDGE,"E2.left"),subQ2])],"isStart":false});Q1=makeQuery(id+"F24.boolean.opBoolean","MERGE",EDGE,{"derivedFrom":[makeQuery(id+"F21.opFillet","BLEND_EDGE",EDGE,{"blendedFrom":[makeQuery(id+"F7.boolean.opBoolean","SPLIT",EDGE,{"disambiguationData":[TD([subQ3])],"derivedFrom":makeQuery(id+"F5.opExtrude","CAP_EDGE",EDGE,{"disambiguationData":[OSD([subQ0])],"isStart":false})}),makeQuery(id+"F7.boolean.opBoolean","SPLIT",FACE,{"disambiguationData":[TD([subQ3])],"derivedFrom":subQ6})],"blendedInto":[makeQuery(id+"F7.boolean.opBoolean","SPLIT",FACE,{"disambiguationData":[TD([subQ3])],"derivedFrom":subQ6})]})],"fromTools":[makeQuery(id+"F24.opExtrude","CAP_EDGE",EDGE,{"disambiguationData":[OSD([sQuery(id+"F23.wireOp",EDGE,"E37.top")])],"isStart":true})]});}
            fillet(context, id + "F25", {"entities" : qUnion([Q0, Q1]), "radius" : 0.5 * mm, "tangentPropagation" : true, "allowEdgeOverflow" : false});
        }
    });
